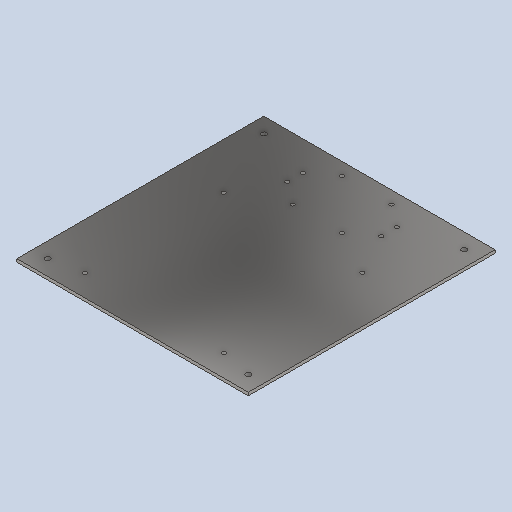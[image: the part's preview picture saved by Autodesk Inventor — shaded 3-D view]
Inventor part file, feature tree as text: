
AUTODESK INVENTOR PART (.ipt)
format: ipt  version: 2023 (Build 270158000, 158)  size: 760,832 bytes
history: native  units: mm
features: sketch x3, hole x2, other x1, extrude x1
ambient origin geometry x8: Origin, YZ Plane, XZ Plane, XY Plane, X Axis, Y Axis, Z Axis, Center Point
bodies: Body1 (feature_tree)
feature tree (7):
  other  "Sólido1"
  extrude  "Extrusão1"  Depth=320.0mm
  hole  "Hole1"  [1 undecoded]
  hole  "Hole2"  [1 undecoded]
  sketch  "Esboço1"  dims[d0=300.0mm d1=320.0mm]
  sketch  "Sketch4"  dims[d2=4.0mm d3=0.0mm d23=20.0mm d25=64.0mm d26=20.0mm d28=64.0mm]
  sketch  "Sketch5"  dims[d32=300.0mm d33=320.0mm d34=5.0mm d35=6.0mm d36=4.0mm d37=2.0mm d38=90.0deg d39=0.5mm d40=20.594885mm d41=16.4mm d42=118.0mm d43=20.0mm d45=122.0mm d46=20.0mm d48=20.0mm d51=38.4mm d52=89.0mm d53=20.0mm d55=180.0mm d56=20.0mm d58=180.0mm d61=60.0mm d62=28.1mm d63=20.0mm d65=280.0mm d66=20.0mm d68=260.0mm d71=320.0mm d72=300.0mm d73=20.0mm d74=20.0mm d75=6.647mm d76=16.0mm d77=4.0mm d78=2.0mm d79=90.0deg d80=8.0mm d81=20.594885mm]
note: 2 required parameter values undecoded (feature->parameter linkage not recoverable at this tier; creation-order binding heuristic only, values carry confidence <= 0.55)
